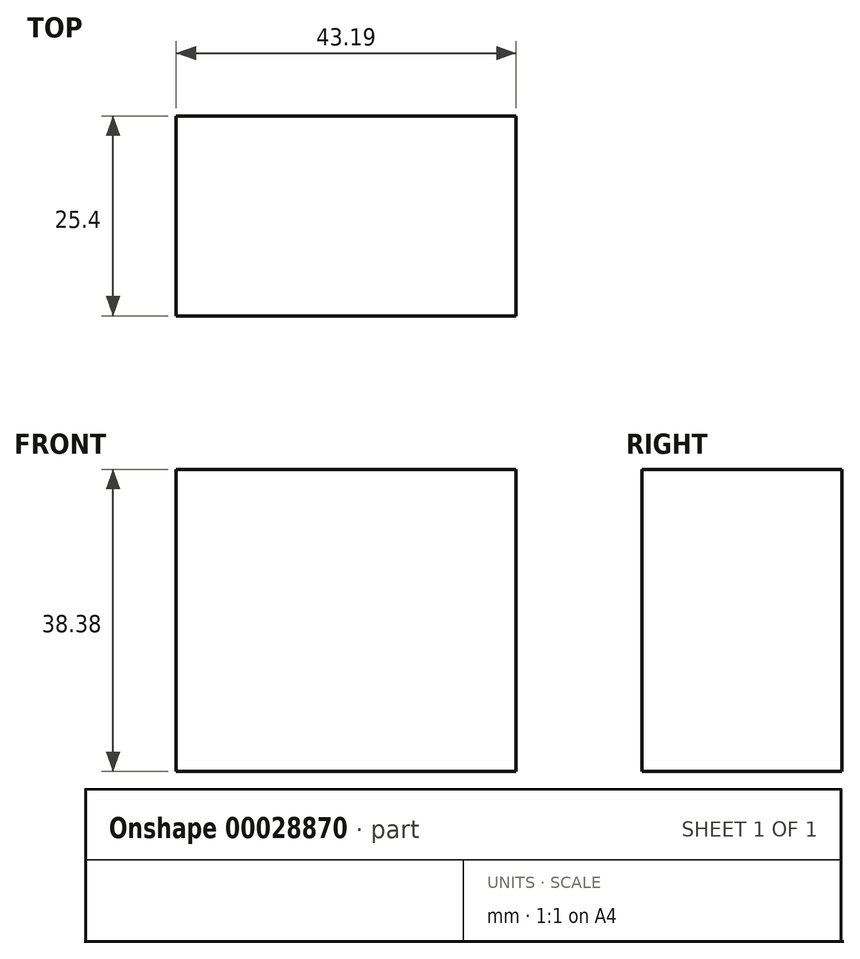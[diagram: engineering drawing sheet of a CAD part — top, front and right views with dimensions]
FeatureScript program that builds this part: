
annotation { "Feature Type Name" : "Feature", "Feature Type Description" : "" }
export const myFeature = defineFeature(function(context is Context, id is Id, definition is map)
    precondition{}
    {
        {
            var Q0;
            Q0=qCreatedBy(makeId("Front.planeOp"),FACE);
            var sketch = newSketch(context, id + "F0", { "sketchPlane" : qUnion([Q0])});
            skLineSegment(sketch, "E0.bottom", {"start": v(-47.87, -58.26) * mm, "end": v(-4.68, -58.26) * mm});
            skLineSegment(sketch, "E0.top", {"start": v(-47.87, -19.88) * mm, "end": v(-4.68, -19.88) * mm});
            skLineSegment(sketch, "E0.left", {"start": v(-47.87, -58.26) * mm, "end": v(-47.87, -19.88) * mm});
            skLineSegment(sketch, "E0.right", {"start": v(-4.68, -58.26) * mm, "end": v(-4.68, -19.88) * mm});
            skSolve(sketch);
        }
        {
            var Q0;
            Q0 = qSketchRegion(id + "F0", true);
            extrude(context, id + "F1", {"entities" : qUnion([Q0]), "depth" : 25.4 * mm});
        }
    });
